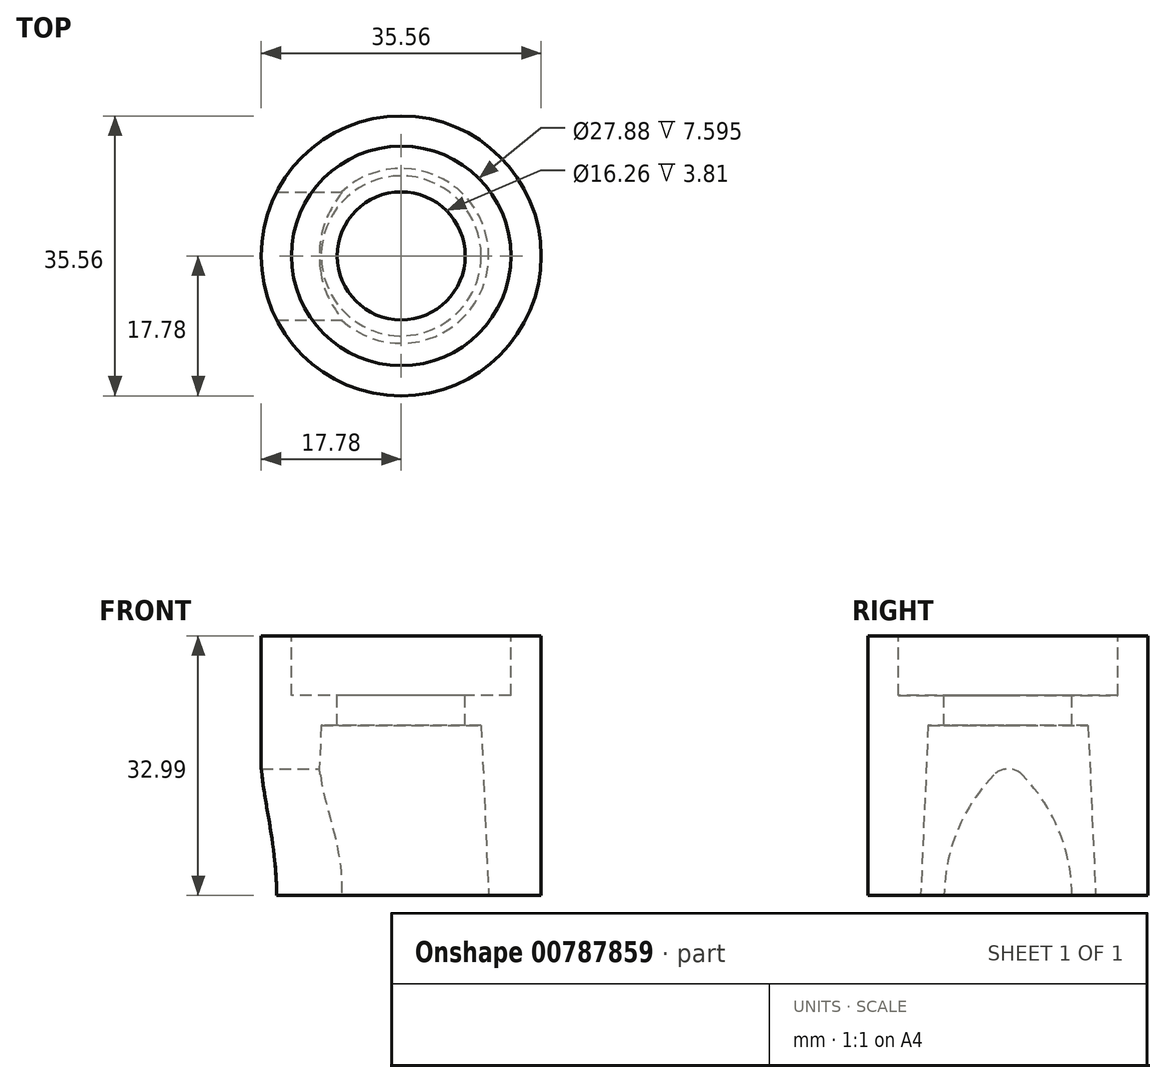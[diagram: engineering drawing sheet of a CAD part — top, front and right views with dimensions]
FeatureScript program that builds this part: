
annotation { "Feature Type Name" : "Feature", "Feature Type Description" : "" }
export const myFeature = defineFeature(function(context is Context, id is Id, definition is map)
    precondition{}
    {
        {
            var Q0;
            Q0=qCreatedBy(makeId("Front.planeOp"),FACE);
            var sketch = newSketch(context, id + "F0", { "sketchPlane" : qUnion([Q0])});
            skLineSegment(sketch, "E0", {"start": v(8.13, 25.4) * mm, "end": v(13.94, 25.4) * mm});
            skLineSegment(sketch, "E1", {"start": v(13.94, 25.4) * mm, "end": v(13.94, 33) * mm});
            skLineSegment(sketch, "E2", {"start": v(13.94, 33) * mm, "end": v(17.78, 33) * mm});
            skLineSegment(sketch, "E3", {"start": v(0, 21.59) * mm, "end": v(0, 0) * mm, "construction": true});
            skLineSegment(sketch, "E4", {"start": v(11.11, 0) * mm, "end": v(10.16, 21.59) * mm});
            skLineSegment(sketch, "E5", {"start": v(10.16, 21.59) * mm, "end": v(8.13, 21.59) * mm});
            skLineSegment(sketch, "E6", {"start": v(0, 21.59) * mm, "end": v(0, 25.4) * mm});
            skLineSegment(sketch, "E7", {"start": v(17.78, 33) * mm, "end": v(17.78, 0) * mm});
            skLineSegment(sketch, "E8", {"start": v(17.78, 0) * mm, "end": v(11.11, 0) * mm});
            skLineSegment(sketch, "E9", {"start": v(8.13, 25.4) * mm, "end": v(8.13, 21.59) * mm});
            skSolve(sketch);
        }
        {
            var Q0;
            Q0=makeQuery(id+"F0.imprint","IMPRINT",FACE,{"disambiguationData":[TD([[makeQuery(id+"F0.imprint","IMPRINT",EDGE,{"derivedFrom":sQuery(id+"F0.wireOp",EDGE,"E0")}),-1.0]])]});
            var Q1;
            Q1=sQuery(id+"F0.wireOp",EDGE,"E3");
            revolve(context, id + "F1", {"surfaceOperationType" : NewSurfaceOperationType.NEW, "entities" : qUnion([Q0]), "axis" : qUnion([Q1]), "revolveType" : RevolveType.FULL});
        }
        {
            var Q0;
            Q0=qCreatedBy(makeId("Right.planeOp"),FACE);
            var sketch = newSketch(context, id + "F2", { "sketchPlane" : qUnion([Q0])});
            skLineSegment(sketch, "E10", {"start": v(0, 17.95) * mm, "end": v(0, 0) * mm, "construction": true});
            skArc(sketch, "E11", {"start": v(-1.83, 15.32) * mm, "mid": v(-6.44, 8.26) * mm, "end": v(-8.13, 0) * mm});
            skArc(sketch, "E12", {"start": v(8.13, 0) * mm, "mid": v(6.44, 8.26) * mm, "end": v(1.83, 15.32) * mm});
            skPoint(sketch, "E13.visualSharp", {"position": v(0, 17.02) * mm});
            skArc(sketch, "E13.filletArc", {"start": v(1.83, 15.32) * mm, "mid": v(0, 16.1) * mm, "end": v(-1.83, 15.32) * mm});
            skLineSegment(sketch, "E14", {"start": v(-8.13, 0) * mm, "end": v(8.13, 0) * mm});
            skSolve(sketch);
        }
        {
            var Q0;
            Q0=makeQuery(id+"F2.imprint","IMPRINT",FACE,{"disambiguationData":[TD([[makeQuery(id+"F2.imprint","IMPRINT",EDGE,{"derivedFrom":sQuery(id+"F2.wireOp",EDGE,"E11")}),1.0]])]});
            extrude(context, id + "F3", {"entities" : qUnion([Q0]), "operationType" : NewBodyOperationType.REMOVE, "oppositeDirection" : true, "depth" : 25.4 * mm, "offsetDistance" : 25.4 * mm});
        }
    });
